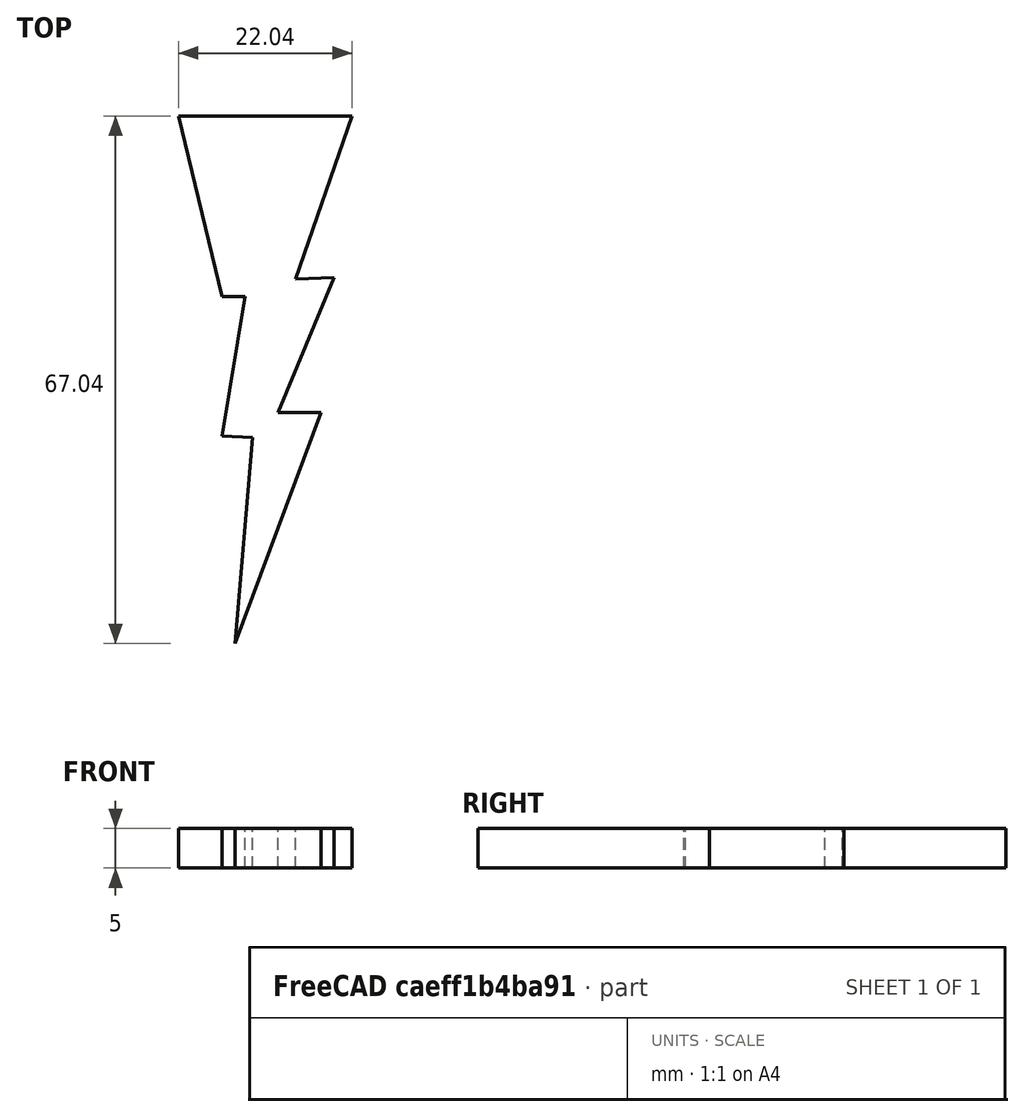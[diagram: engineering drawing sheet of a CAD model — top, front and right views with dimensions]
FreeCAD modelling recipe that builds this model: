
FCSTD DOCUMENT  (FreeCAD 1.0R39319 (Git))
Label: Sense ojt1_t16r03_ray
License: All rights reserved
LicenseURL: https://en.wikipedia.org/wiki/All_rights_reserved
objects: Sketcher::SketchObject×1, PartDesign::Pad×1, PartDesign::Body×1
note: 6 computed .brp shape members not serialized (recipe doc carries the construction recipe); baked Part::Feature solids carry a one-line shape summary decoded from their .brp

FEATURE [Sketcher::SketchObject] Sketch
  ArcFitTolerance = 1e-06
  AttachmentSupport = -> [XY_Plane]
  FullyConstrained = false
  MakeInternals = false
  MapMode = 5
  sketch-geometry (11):
    g0: LineSegment StartX=-5.5556 StartY=39.4539 StartZ=0 EndX=16.4783 EndY=39.4539 EndZ=0
    g1: LineSegment StartX=16.4783 StartY=39.4539 StartZ=0 EndX=9.32199 EndY=18.7383 EndZ=0
    g2: LineSegment StartX=9.32199 StartY=18.7383 StartZ=0 EndX=14.2184 EndY=18.9266 EndZ=0
    g3: LineSegment StartX=14.2184 StartY=18.9266 StartZ=0 EndX=7.0621 EndY=1.78912 EndZ=0
    g4: LineSegment StartX=7.0621 StartY=1.78912 StartZ=0 EndX=12.5235 EndY=1.78912 EndZ=0
    g5: LineSegment StartX=12.5235 StartY=1.78912 StartZ=0 EndX=1.60071 EndY=-27.5894 EndZ=0
    g6: LineSegment StartX=1.60071 StartY=-27.5894 StartZ=0 EndX=3.86059 EndY=-1.41238 EndZ=0
    g7: LineSegment StartX=3.86059 StartY=-1.41238 StartZ=0 EndX=0 EndY=-1.22406 EndZ=0
    g8: LineSegment StartX=0 StartY=-1.22406 StartZ=0 EndX=2.91898 EndY=16.4784 EndZ=0
    g9: LineSegment StartX=2.91898 StartY=16.4784 StartZ=0 EndX=0 EndY=16.4784 EndZ=0
    g10: LineSegment StartX=0 StartY=16.4784 StartZ=0 EndX=-5.5556 EndY=39.4539 EndZ=0
  constraints (16):
    c: Horizontal(g0)
    c: Coincident(g0,g1)
    c: Coincident(g1,g2)
    c: Coincident(g2,g3)
    c: Coincident(g3,g4)
    c: Horizontal(g4)
    c: Coincident(g4,g5)
    c: Coincident(g5,g6)
    c: Coincident(g6,g7)
    c: PointOnObject(g7,g-2)
    c: Coincident(g7,g8)
    c: Coincident(g8,g9)
    c: PointOnObject(g9,g-2)
    c: Horizontal(g9)
    c: Coincident(g9,g10)
    c: Coincident(g10,g0)
FEATURE [PartDesign::Pad] Pad
  Direction = (0,0,1)
  Length = 5
  Length2 = 10
  Profile = -> Sketch
  ReferenceAxis = -> Sketch [N_Axis]
  Refine = true
  Suppressed = false
  Type = 0
FEATURE [PartDesign::Body] Body  label="Cos"
  AllowCompound = false
  Group = -> [Sketch,Pad]
  Origin = -> Origin
  Tip = -> Pad
